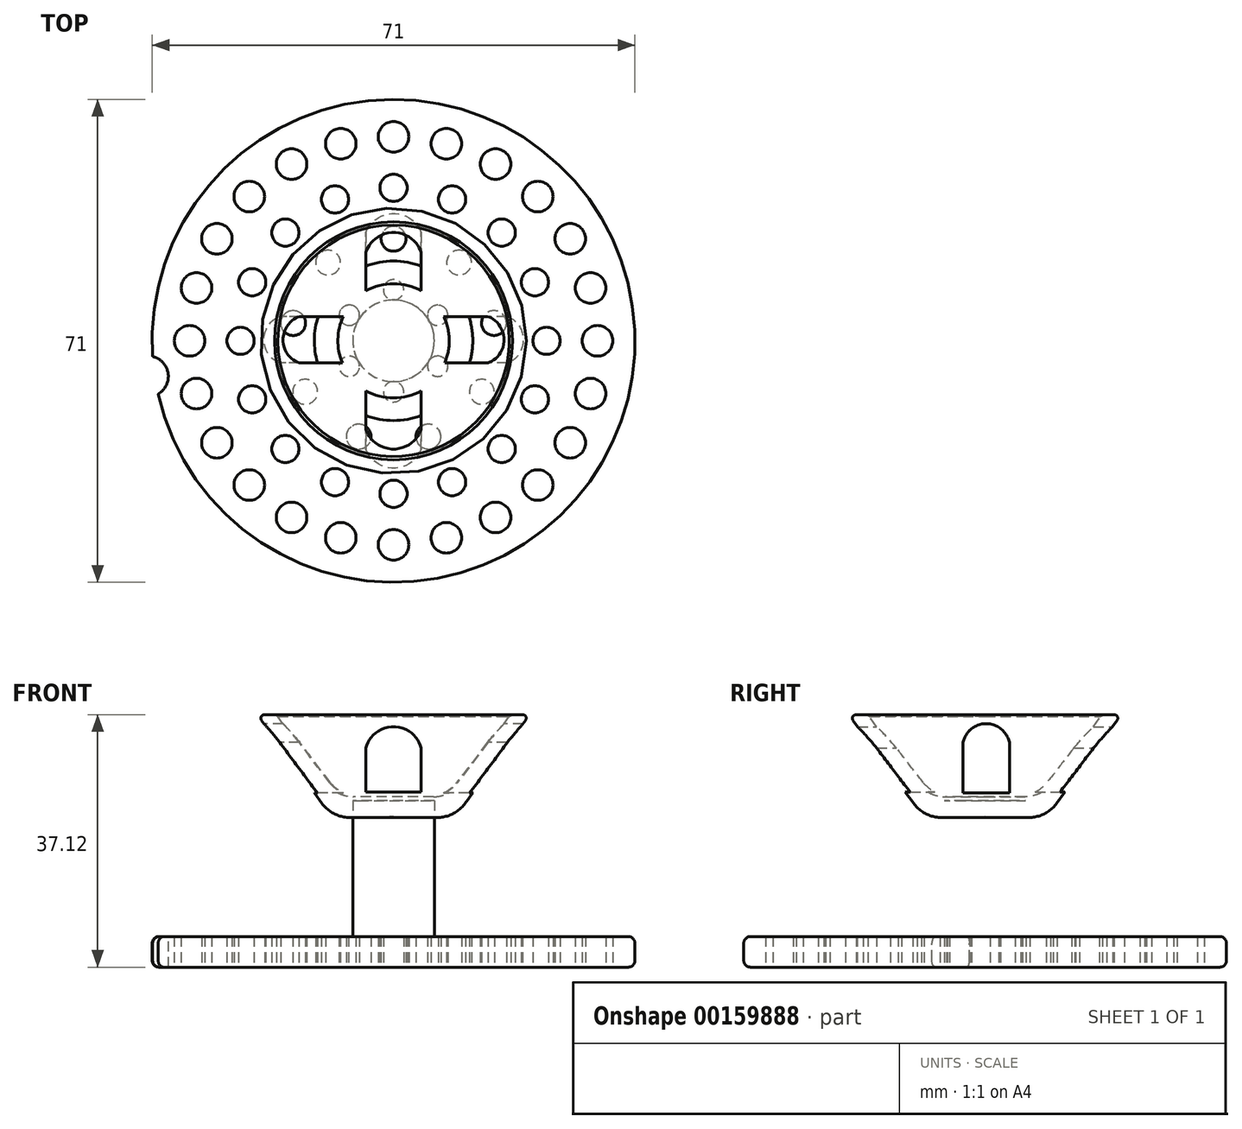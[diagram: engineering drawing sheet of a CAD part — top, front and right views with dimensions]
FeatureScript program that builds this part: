
annotation { "Feature Type Name" : "Feature", "Feature Type Description" : "" }
export const myFeature = defineFeature(function(context is Context, id is Id, definition is map)
    precondition{}
    {
        {
            var Q0;
            Q0=qCreatedBy(makeId("Top.planeOp"),FACE);
            var sketch = newSketch(context, id + "F0", { "sketchPlane" : qUnion([Q0])});
            skCircle(sketch, "E0", {"center": v(0, 0) * mm, "radius": 35.5 * mm});
            skSolve(sketch);
        }
        {
            var Q0;
            Q0=makeQuery(id+"F0.imprint","IMPRINT",FACE,{"disambiguationData":[TD([[makeQuery(id+"F0.imprint","IMPRINT",EDGE,{"derivedFrom":sQuery(id+"F0.wireOp",EDGE,"E0")}),1.0]])]});
            var sketch = newSketch(context, id + "F1", { "sketchPlane" : qUnion([Q0])});
            skCircle(sketch, "E1", {"center": v(0, 0) * mm, "radius": 7.5 * mm, "construction": true});
            skCircle(sketch, "E2", {"center": v(0, 7.5) * mm, "radius": 1.5 * mm});
            skCircle(sketch, "E3.1.1", {"center": v(-6.5, 3.75) * mm, "radius": 1.5 * mm});
            skCircle(sketch, "E3.2.1", {"center": v(-6.5, -3.75) * mm, "radius": 1.5 * mm});
            skCircle(sketch, "E3.3.1", {"center": v(0, -7.5) * mm, "radius": 1.5 * mm});
            skCircle(sketch, "E3.4.1", {"center": v(6.5, -3.75) * mm, "radius": 1.5 * mm});
            skCircle(sketch, "E3.5.1", {"center": v(6.5, 3.75) * mm, "radius": 1.5 * mm});
            skSolve(sketch);
        }
        {
            var Q0;
            Q0=makeQuery(id+"F0.imprint","IMPRINT",FACE,{"disambiguationData":[TD([[makeQuery(id+"F0.imprint","IMPRINT",EDGE,{"derivedFrom":sQuery(id+"F0.wireOp",EDGE,"E0")}),1.0]])]});
            var sketch = newSketch(context, id + "F2", { "sketchPlane" : qUnion([Q0])});
            skCircle(sketch, "E4", {"center": v(0, 0) * mm, "radius": 15 * mm, "construction": true});
            skCircle(sketch, "E5", {"center": v(0, 15) * mm, "radius": 1.83 * mm});
            skCircle(sketch, "E6.1.0", {"center": v(-9.64, 11.5) * mm, "radius": 1.83 * mm});
            skCircle(sketch, "E6.2.0", {"center": v(-14.77, 2.6) * mm, "radius": 1.83 * mm});
            skCircle(sketch, "E6.3.0", {"center": v(-13, -7.5) * mm, "radius": 1.83 * mm});
            skCircle(sketch, "E6.4.0", {"center": v(-5.13, -14.1) * mm, "radius": 1.83 * mm});
            skCircle(sketch, "E6.5.0", {"center": v(5.13, -14.1) * mm, "radius": 1.83 * mm});
            skCircle(sketch, "E6.6.0", {"center": v(13, -7.5) * mm, "radius": 1.83 * mm});
            skCircle(sketch, "E6.7.0", {"center": v(14.77, 2.6) * mm, "radius": 1.83 * mm});
            skCircle(sketch, "E6.8.0", {"center": v(9.64, 11.5) * mm, "radius": 1.83 * mm});
            skSolve(sketch);
        }
        {
            var Q0;
            Q0=makeQuery(id+"F0.imprint","IMPRINT",FACE,{"disambiguationData":[TD([[makeQuery(id+"F0.imprint","IMPRINT",EDGE,{"derivedFrom":sQuery(id+"F0.wireOp",EDGE,"E0")}),1.0]])]});
            var sketch = newSketch(context, id + "F3", { "sketchPlane" : qUnion([Q0])});
            skCircle(sketch, "E7", {"center": v(0, 0) * mm, "radius": 22.5 * mm, "construction": true});
            skCircle(sketch, "E8", {"center": v(0, 22.5) * mm, "radius": 2 * mm});
            skCircle(sketch, "E9.1.0", {"center": v(-8.61, 20.79) * mm, "radius": 2 * mm});
            skCircle(sketch, "E9.2.0", {"center": v(-15.9, 15.9) * mm, "radius": 2 * mm});
            skCircle(sketch, "E9.3.0", {"center": v(-20.79, 8.61) * mm, "radius": 2 * mm});
            skCircle(sketch, "E9.4.0", {"center": v(-22.5, 0) * mm, "radius": 2 * mm});
            skCircle(sketch, "E9.5.0", {"center": v(-20.79, -8.61) * mm, "radius": 2 * mm});
            skCircle(sketch, "E9.6.0", {"center": v(-15.9, -15.9) * mm, "radius": 2 * mm});
            skCircle(sketch, "E9.7.0", {"center": v(-8.61, -20.79) * mm, "radius": 2 * mm});
            skCircle(sketch, "E9.8.0", {"center": v(0, -22.5) * mm, "radius": 2 * mm});
            skCircle(sketch, "E9.9.0", {"center": v(8.61, -20.79) * mm, "radius": 2 * mm});
            skCircle(sketch, "E9.10.0", {"center": v(15.9, -15.9) * mm, "radius": 2 * mm});
            skCircle(sketch, "E9.11.0", {"center": v(20.79, -8.61) * mm, "radius": 2 * mm});
            skCircle(sketch, "E9.12.0", {"center": v(22.5, 0) * mm, "radius": 2 * mm});
            skCircle(sketch, "E9.13.0", {"center": v(20.79, 8.61) * mm, "radius": 2 * mm});
            skCircle(sketch, "E9.14.0", {"center": v(15.9, 15.9) * mm, "radius": 2 * mm});
            skCircle(sketch, "E9.15.0", {"center": v(8.61, 20.79) * mm, "radius": 2 * mm});
            skSolve(sketch);
        }
        {
            var Q0;
            Q0=makeQuery(id+"F0.imprint","IMPRINT",FACE,{"disambiguationData":[TD([[makeQuery(id+"F0.imprint","IMPRINT",EDGE,{"derivedFrom":sQuery(id+"F0.wireOp",EDGE,"E0")}),1.0]])]});
            var sketch = newSketch(context, id + "F4", { "sketchPlane" : qUnion([Q0])});
            skCircle(sketch, "E10", {"center": v(0, 0) * mm, "radius": 30 * mm, "construction": true});
            skCircle(sketch, "E11", {"center": v(0, 30) * mm, "radius": 2.25 * mm});
            skCircle(sketch, "E12.1.0", {"center": v(-7.76, 28.98) * mm, "radius": 2.25 * mm});
            skCircle(sketch, "E12.2.0", {"center": v(-15, 25.98) * mm, "radius": 2.25 * mm});
            skCircle(sketch, "E13.1.3.0", {"center": v(-21.21, 21.21) * mm, "radius": 2.25 * mm});
            skCircle(sketch, "E13.1.4.0", {"center": v(-25.98, 15) * mm, "radius": 2.25 * mm});
            skCircle(sketch, "E13.1.5.0", {"center": v(-28.98, 7.76) * mm, "radius": 2.25 * mm});
            skCircle(sketch, "E13.1.6.0", {"center": v(-30, 0) * mm, "radius": 2.25 * mm});
            skCircle(sketch, "E13.1.7.0", {"center": v(-28.98, -7.76) * mm, "radius": 2.25 * mm});
            skCircle(sketch, "E13.1.8.0", {"center": v(-25.98, -15) * mm, "radius": 2.25 * mm});
            skCircle(sketch, "E13.1.9.0", {"center": v(-21.21, -21.21) * mm, "radius": 2.25 * mm});
            skCircle(sketch, "E13.1.10.0", {"center": v(-15, -25.98) * mm, "radius": 2.25 * mm});
            skCircle(sketch, "E13.1.11.0", {"center": v(-7.76, -28.98) * mm, "radius": 2.25 * mm});
            skCircle(sketch, "E13.1.12.0", {"center": v(0, -30) * mm, "radius": 2.25 * mm});
            skCircle(sketch, "E13.1.13.0", {"center": v(7.76, -28.98) * mm, "radius": 2.25 * mm});
            skCircle(sketch, "E13.1.14.0", {"center": v(15, -25.98) * mm, "radius": 2.25 * mm});
            skCircle(sketch, "E13.1.15.0", {"center": v(21.21, -21.21) * mm, "radius": 2.25 * mm});
            skCircle(sketch, "E13.1.16.0", {"center": v(25.98, -15) * mm, "radius": 2.25 * mm});
            skCircle(sketch, "E13.1.17.0", {"center": v(28.98, -7.76) * mm, "radius": 2.25 * mm});
            skCircle(sketch, "E13.1.18.0", {"center": v(30, 0) * mm, "radius": 2.25 * mm});
            skCircle(sketch, "E13.1.19.0", {"center": v(28.98, 7.76) * mm, "radius": 2.25 * mm});
            skCircle(sketch, "E13.1.20.0", {"center": v(25.98, 15) * mm, "radius": 2.25 * mm});
            skCircle(sketch, "E13.1.21.0", {"center": v(21.21, 21.21) * mm, "radius": 2.25 * mm});
            skCircle(sketch, "E13.1.22.0", {"center": v(15, 25.98) * mm, "radius": 2.25 * mm});
            skCircle(sketch, "E13.1.23.0", {"center": v(7.76, 28.98) * mm, "radius": 2.25 * mm});
            skSolve(sketch);
        }
        {
            var Q0;
            Q0=qSketchRegion(id+"F4",true);
            extrude(context, id + "F5", {"entities" : qUnion([Q0]), "depth" : 5 * mm});
        }
        {
            var Q0;
            Q0=qSketchRegion(id+"F3",true);
            extrude(context, id + "F6", {"entities" : qUnion([Q0]), "depth" : 5 * mm});
        }
        {
            var Q0;
            Q0=qSketchRegion(id+"F2",true);
            extrude(context, id + "F7", {"entities" : qUnion([Q0]), "depth" : 5 * mm});
        }
        {
            var Q0;
            Q0=qSketchRegion(id+"F1",true);
            extrude(context, id + "F8", {"entities" : qUnion([Q0]), "depth" : 5 * mm});
        }
        {
            var Q0;
            Q0=qSketchRegion(id+"F0",true);
            extrude(context, id + "F9", {"entities" : qUnion([Q0]), "depth" : 4.5 * mm});
        }
        {
            var Q0;
            Q0=makeQuery(id+"F5.opExtrude","SWEPT_BODY",BODY,{"disambiguationData":[OSD([sQuery(id+"F4.wireOp",EDGE,"E11")])]});
            var Q1;
            Q1=makeQuery(id+"F5.opExtrude","SWEPT_BODY",BODY,{"disambiguationData":[OSD([sQuery(id+"F4.wireOp",EDGE,"E13.1.3.0")])]});
            var Q2;
            Q2=makeQuery(id+"F5.opExtrude","SWEPT_BODY",BODY,{"disambiguationData":[OSD([sQuery(id+"F4.wireOp",EDGE,"E13.1.7.0")])]});
            var Q3;
            Q3=makeQuery(id+"F5.opExtrude","SWEPT_BODY",BODY,{"disambiguationData":[OSD([sQuery(id+"F4.wireOp",EDGE,"E12.1.0")])]});
            var Q4;
            Q4=makeQuery(id+"F5.opExtrude","SWEPT_BODY",BODY,{"disambiguationData":[OSD([sQuery(id+"F4.wireOp",EDGE,"E12.2.0")])]});
            var Q5;
            Q5=makeQuery(id+"F5.opExtrude","SWEPT_BODY",BODY,{"disambiguationData":[OSD([sQuery(id+"F4.wireOp",EDGE,"E13.1.4.0")])]});
            var Q6;
            Q6=makeQuery(id+"F5.opExtrude","SWEPT_BODY",BODY,{"disambiguationData":[OSD([sQuery(id+"F4.wireOp",EDGE,"E13.1.5.0")])]});
            var Q7;
            Q7=makeQuery(id+"F5.opExtrude","SWEPT_BODY",BODY,{"disambiguationData":[OSD([sQuery(id+"F4.wireOp",EDGE,"E13.1.6.0")])]});
            var Q8;
            Q8=makeQuery(id+"F5.opExtrude","SWEPT_BODY",BODY,{"disambiguationData":[OSD([sQuery(id+"F4.wireOp",EDGE,"E13.1.8.0")])]});
            var Q9;
            Q9=makeQuery(id+"F5.opExtrude","SWEPT_BODY",BODY,{"disambiguationData":[OSD([sQuery(id+"F4.wireOp",EDGE,"E13.1.9.0")])]});
            var Q10;
            Q10=makeQuery(id+"F5.opExtrude","SWEPT_BODY",BODY,{"disambiguationData":[OSD([sQuery(id+"F4.wireOp",EDGE,"E13.1.10.0")])]});
            var Q11;
            Q11=makeQuery(id+"F5.opExtrude","SWEPT_BODY",BODY,{"disambiguationData":[OSD([sQuery(id+"F4.wireOp",EDGE,"E13.1.11.0")])]});
            var Q12;
            Q12=makeQuery(id+"F5.opExtrude","SWEPT_BODY",BODY,{"disambiguationData":[OSD([sQuery(id+"F4.wireOp",EDGE,"E13.1.12.0")])]});
            var Q13;
            Q13=makeQuery(id+"F5.opExtrude","SWEPT_BODY",BODY,{"disambiguationData":[OSD([sQuery(id+"F4.wireOp",EDGE,"E13.1.13.0")])]});
            var Q14;
            Q14=makeQuery(id+"F5.opExtrude","SWEPT_BODY",BODY,{"disambiguationData":[OSD([sQuery(id+"F4.wireOp",EDGE,"E13.1.14.0")])]});
            var Q15;
            Q15=makeQuery(id+"F5.opExtrude","SWEPT_BODY",BODY,{"disambiguationData":[OSD([sQuery(id+"F4.wireOp",EDGE,"E13.1.15.0")])]});
            var Q16;
            Q16=makeQuery(id+"F5.opExtrude","SWEPT_BODY",BODY,{"disambiguationData":[OSD([sQuery(id+"F4.wireOp",EDGE,"E13.1.16.0")])]});
            var Q17;
            Q17=makeQuery(id+"F5.opExtrude","SWEPT_BODY",BODY,{"disambiguationData":[OSD([sQuery(id+"F4.wireOp",EDGE,"E13.1.17.0")])]});
            var Q18;
            Q18=makeQuery(id+"F5.opExtrude","SWEPT_BODY",BODY,{"disambiguationData":[OSD([sQuery(id+"F4.wireOp",EDGE,"E13.1.18.0")])]});
            var Q19;
            Q19=makeQuery(id+"F5.opExtrude","SWEPT_BODY",BODY,{"disambiguationData":[OSD([sQuery(id+"F4.wireOp",EDGE,"E13.1.19.0")])]});
            var Q20;
            Q20=makeQuery(id+"F5.opExtrude","SWEPT_BODY",BODY,{"disambiguationData":[OSD([sQuery(id+"F4.wireOp",EDGE,"E13.1.20.0")])]});
            var Q21;
            Q21=makeQuery(id+"F5.opExtrude","SWEPT_BODY",BODY,{"disambiguationData":[OSD([sQuery(id+"F4.wireOp",EDGE,"E13.1.21.0")])]});
            var Q22;
            Q22=makeQuery(id+"F5.opExtrude","SWEPT_BODY",BODY,{"disambiguationData":[OSD([sQuery(id+"F4.wireOp",EDGE,"E13.1.22.0")])]});
            var Q23;
            Q23=makeQuery(id+"F5.opExtrude","SWEPT_BODY",BODY,{"disambiguationData":[OSD([sQuery(id+"F4.wireOp",EDGE,"E13.1.23.0")])]});
            var Q24;
            Q24=makeQuery(id+"F6.opExtrude","SWEPT_BODY",BODY,{"disambiguationData":[OSD([sQuery(id+"F3.wireOp",EDGE,"E9.15.0")])]});
            var Q25;
            Q25=makeQuery(id+"F6.opExtrude","SWEPT_BODY",BODY,{"disambiguationData":[OSD([sQuery(id+"F3.wireOp",EDGE,"E8")])]});
            var Q26;
            Q26=makeQuery(id+"F6.opExtrude","SWEPT_BODY",BODY,{"disambiguationData":[OSD([sQuery(id+"F3.wireOp",EDGE,"E9.1.0")])]});
            var Q27;
            Q27=makeQuery(id+"F6.opExtrude","SWEPT_BODY",BODY,{"disambiguationData":[OSD([sQuery(id+"F3.wireOp",EDGE,"E9.2.0")])]});
            var Q28;
            Q28=makeQuery(id+"F6.opExtrude","SWEPT_BODY",BODY,{"disambiguationData":[OSD([sQuery(id+"F3.wireOp",EDGE,"E9.3.0")])]});
            var Q29;
            Q29=makeQuery(id+"F6.opExtrude","SWEPT_BODY",BODY,{"disambiguationData":[OSD([sQuery(id+"F3.wireOp",EDGE,"E9.4.0")])]});
            var Q30;
            Q30=makeQuery(id+"F6.opExtrude","SWEPT_BODY",BODY,{"disambiguationData":[OSD([sQuery(id+"F3.wireOp",EDGE,"E9.5.0")])]});
            var Q31;
            Q31=makeQuery(id+"F6.opExtrude","SWEPT_BODY",BODY,{"disambiguationData":[OSD([sQuery(id+"F3.wireOp",EDGE,"E9.6.0")])]});
            var Q32;
            Q32=makeQuery(id+"F6.opExtrude","SWEPT_BODY",BODY,{"disambiguationData":[OSD([sQuery(id+"F3.wireOp",EDGE,"E9.7.0")])]});
            var Q33;
            Q33=makeQuery(id+"F6.opExtrude","SWEPT_BODY",BODY,{"disambiguationData":[OSD([sQuery(id+"F3.wireOp",EDGE,"E9.8.0")])]});
            var Q34;
            Q34=makeQuery(id+"F6.opExtrude","SWEPT_BODY",BODY,{"disambiguationData":[OSD([sQuery(id+"F3.wireOp",EDGE,"E9.9.0")])]});
            var Q35;
            Q35=makeQuery(id+"F6.opExtrude","SWEPT_BODY",BODY,{"disambiguationData":[OSD([sQuery(id+"F3.wireOp",EDGE,"E9.10.0")])]});
            var Q36;
            Q36=makeQuery(id+"F6.opExtrude","SWEPT_BODY",BODY,{"disambiguationData":[OSD([sQuery(id+"F3.wireOp",EDGE,"E9.11.0")])]});
            var Q37;
            Q37=makeQuery(id+"F6.opExtrude","SWEPT_BODY",BODY,{"disambiguationData":[OSD([sQuery(id+"F3.wireOp",EDGE,"E9.12.0")])]});
            var Q38;
            Q38=makeQuery(id+"F6.opExtrude","SWEPT_BODY",BODY,{"disambiguationData":[OSD([sQuery(id+"F3.wireOp",EDGE,"E9.13.0")])]});
            var Q39;
            Q39=makeQuery(id+"F6.opExtrude","SWEPT_BODY",BODY,{"disambiguationData":[OSD([sQuery(id+"F3.wireOp",EDGE,"E9.14.0")])]});
            var Q40;
            Q40=makeQuery(id+"F7.opExtrude","SWEPT_BODY",BODY,{"disambiguationData":[OSD([sQuery(id+"F2.wireOp",EDGE,"E6.8.0")])]});
            var Q41;
            Q41=makeQuery(id+"F7.opExtrude","SWEPT_BODY",BODY,{"disambiguationData":[OSD([sQuery(id+"F2.wireOp",EDGE,"E6.7.0")])]});
            var Q42;
            Q42=makeQuery(id+"F7.opExtrude","SWEPT_BODY",BODY,{"disambiguationData":[OSD([sQuery(id+"F2.wireOp",EDGE,"E6.6.0")])]});
            var Q43;
            Q43=makeQuery(id+"F7.opExtrude","SWEPT_BODY",BODY,{"disambiguationData":[OSD([sQuery(id+"F2.wireOp",EDGE,"E6.5.0")])]});
            var Q44;
            Q44=makeQuery(id+"F7.opExtrude","SWEPT_BODY",BODY,{"disambiguationData":[OSD([sQuery(id+"F2.wireOp",EDGE,"E6.4.0")])]});
            var Q45;
            Q45=makeQuery(id+"F7.opExtrude","SWEPT_BODY",BODY,{"disambiguationData":[OSD([sQuery(id+"F2.wireOp",EDGE,"E6.3.0")])]});
            var Q46;
            Q46=makeQuery(id+"F7.opExtrude","SWEPT_BODY",BODY,{"disambiguationData":[OSD([sQuery(id+"F2.wireOp",EDGE,"E6.2.0")])]});
            var Q47;
            Q47=makeQuery(id+"F7.opExtrude","SWEPT_BODY",BODY,{"disambiguationData":[OSD([sQuery(id+"F2.wireOp",EDGE,"E6.1.0")])]});
            var Q48;
            Q48=makeQuery(id+"F7.opExtrude","SWEPT_BODY",BODY,{"disambiguationData":[OSD([sQuery(id+"F2.wireOp",EDGE,"E5")])]});
            var Q49;
            Q49=makeQuery(id+"F8.opExtrude","SWEPT_BODY",BODY,{"disambiguationData":[OSD([sQuery(id+"F1.wireOp",EDGE,"E2")])]});
            var Q50;
            Q50=makeQuery(id+"F8.opExtrude","SWEPT_BODY",BODY,{"disambiguationData":[OSD([sQuery(id+"F1.wireOp",EDGE,"E3.5.1")])]});
            var Q51;
            Q51=makeQuery(id+"F8.opExtrude","SWEPT_BODY",BODY,{"disambiguationData":[OSD([sQuery(id+"F1.wireOp",EDGE,"E3.4.1")])]});
            var Q52;
            Q52=makeQuery(id+"F8.opExtrude","SWEPT_BODY",BODY,{"disambiguationData":[OSD([sQuery(id+"F1.wireOp",EDGE,"E3.3.1")])]});
            var Q53;
            Q53=makeQuery(id+"F8.opExtrude","SWEPT_BODY",BODY,{"disambiguationData":[OSD([sQuery(id+"F1.wireOp",EDGE,"E3.2.1")])]});
            var Q54;
            Q54=makeQuery(id+"F8.opExtrude","SWEPT_BODY",BODY,{"disambiguationData":[OSD([sQuery(id+"F1.wireOp",EDGE,"E3.1.1")])]});
            var Q55;
            Q55=makeQuery(id+"F9.opExtrude","SWEPT_BODY",BODY,{"disambiguationData":[OSD([sQuery(id+"F0.wireOp",EDGE,"E0")])]});
            booleanBodies(context, id + "F10", {"operationType" : BooleanOperationType.SUBTRACTION, "tools" : qUnion([Q0, Q1, Q2, Q3, Q4, Q5, Q6, Q7, Q8, Q9, Q10, Q11, Q12, Q13, Q14, Q15, Q16, Q17, Q18, Q19, Q20, Q21, Q22, Q23, Q24, Q25, Q26, Q27, Q28, Q29, Q30, Q31, Q32, Q33, Q34, Q35, Q36, Q37, Q38, Q39, Q40, Q41, Q42, Q43, Q44, Q45, Q46, Q47, Q48, Q49, Q50, Q51, Q52, Q53, Q54]), "targets" : qUnion([Q55])});
        }
        {
            var Q0;
            Q0=makeQuery(id+"F9.opExtrude","CAP_EDGE",EDGE,{"disambiguationData":[OSD([sQuery(id+"F0.wireOp",EDGE,"E0")])],"isStart":true});
            var Q1;
            Q1=makeQuery(id+"F9.opExtrude","CAP_EDGE",EDGE,{"disambiguationData":[OSD([sQuery(id+"F0.wireOp",EDGE,"E0")])],"isStart":false});
            fillet(context, id + "F11", {"entities" : qUnion([Q0, Q1]), "radius" : 1 * mm, "tangentPropagation" : true, "allowEdgeOverflow" : false});
        }
        {
            var Q0;
            Q0=makeQuery(id+"F9.opExtrude","CAP_FACE",FACE,{"disambiguationData":[OSD([sQuery(id+"F0.wireOp",EDGE,"E0")])],"isStart":false});
            var sketch = newSketch(context, id + "F12", { "sketchPlane" : qUnion([Q0])});
            skCircle(sketch, "E14", {"center": v(0, 0) * mm, "radius": 6 * mm});
            skSolve(sketch);
        }
        {
            var Q0;
            Q0=makeQuery(id+"F12.imprint","IMPRINT",FACE,{"disambiguationData":[TD([[makeQuery(id+"F12.imprint","IMPRINT",EDGE,{"derivedFrom":sQuery(id+"F12.wireOp",EDGE,"E14")}),1.0]])]});
            extrude(context, id + "F13", {"entities" : qUnion([Q0]), "operationType" : NewBodyOperationType.ADD, "depth" : 20 * mm, "offsetDistance" : 25 * mm});
        }
        {
            var Q0;
            Q0=makeQuery(id+"F9.opExtrude","CAP_FACE",FACE,{"disambiguationData":[OSD([sQuery(id+"F0.wireOp",EDGE,"E0")])],"isStart":false});
            var sketch = newSketch(context, id + "F14", { "sketchPlane" : qUnion([Q0])});
            skCircle(sketch, "E15", {"center": v(0, 0) * mm, "radius": 36.5 * mm, "construction": true});
            skCircle(sketch, "E16", {"center": v(-36.12, -5.23) * mm, "radius": 3 * mm});
            skSolve(sketch);
        }
        {
            var Q0;
            Q0=makeQuery(id+"F14.imprint","IMPRINT",FACE,{"disambiguationData":[TD([[makeQuery(id+"F14.imprint","IMPRINT",EDGE,{"derivedFrom":sQuery(id+"F14.wireOp",EDGE,"E16")}),1.0]])]});
            extrude(context, id + "F15", {"entities" : qUnion([Q0]), "operationType" : NewBodyOperationType.REMOVE, "oppositeDirection" : true, "depth" : 25 * mm});
        }
        {
            var Q0;
            Q0=qCreatedBy(makeId("Front.planeOp"),FACE);
            var sketch = newSketch(context, id + "F16", { "sketchPlane" : qUnion([Q0])});
            skLineSegment(sketch, "E17", {"start": v(0, 64.6) * mm, "end": v(0, 86.12) * mm, "construction": true});
            skLineSegment(sketch, "E18", {"start": v(-20, 85.12) * mm, "end": v(-9, 69.99) * mm});
            skLineSegment(sketch, "E19", {"start": v(0, 70.12) * mm, "end": v(0, 86.12) * mm});
            skLineSegment(sketch, "E20", {"start": v(-20, 85.12) * mm, "end": v(-17.2, 85.12) * mm});
            skLineSegment(sketch, "E21", {"start": v(-17.2, 85.12) * mm, "end": v(-8.44, 73.07) * mm});
            skLineSegment(sketch, "E22", {"start": v(-8.44, 73.07) * mm, "end": v(0, 73.07) * mm});
            skLineSegment(sketch, "E23", {"start": v(-9, 69.99) * mm, "end": v(0, 70.12) * mm});
            skSolve(sketch);
        }
        {
            var Q0;
            Q0=makeQuery(id+"F16.imprint","IMPRINT",FACE,{"disambiguationData":[TD([[makeQuery(id+"F16.imprint","IMPRINT",EDGE,{"derivedFrom":sQuery(id+"F16.wireOp",EDGE,"E18")}),1.0]])]});
            var Q1;
            Q1=sQuery(id+"F16.wireOp",EDGE,"E19");
            revolve(context, id + "F17", {"operationType" : NewBodyOperationType.ADD, "surfaceOperationType" : NewSurfaceOperationType.NEW, "entities" : qUnion([Q0]), "axis" : qUnion([Q1]), "revolveType" : RevolveType.FULL});
        }
        {
            var Q0;
            Q0=makeQuery(id+"F17.opRevolve","SWEPT_BODY",BODY,{"disambiguationData":[OSD([sQuery(id+"F16.wireOp",EDGE,"E18"),sQuery(id+"F16.wireOp",EDGE,"ekqP7qBP-ulQC-kSXt-n5Og-ePe3p9eNB1yX"),sQuery(id+"F16.wireOp",EDGE,"E19"),sQuery(id+"F16.wireOp",EDGE,"E20"),sQuery(id+"F16.wireOp",EDGE,"E21"),sQuery(id+"F16.wireOp",EDGE,"E22")])]});
            transform(context, id + "F18", {"entities" : qUnion([Q0]), "transformType" : TransformType.TRANSLATION_3D, "dx" : 0 * mm, "dy" : 0 * mm, "dz" : -48 * mm, "makeCopy" : false});
        }
        {
            var Q0;
            Q0=qCreatedBy(makeId("Front.planeOp"),FACE);
            var sketch = newSketch(context, id + "F19", { "sketchPlane" : qUnion([Q0])});
            skLineSegment(sketch, "E24.bottom", {"start": v(4.06, 25.75) * mm, "end": v(-4.06, 25.75) * mm});
            skLineSegment(sketch, "E24.top", {"start": v(4.06, 32.22) * mm, "end": v(-4.06, 32.22) * mm});
            skLineSegment(sketch, "E24.left", {"start": v(4.06, 25.75) * mm, "end": v(4.06, 32.22) * mm});
            skLineSegment(sketch, "E24.right", {"start": v(-4.06, 25.75) * mm, "end": v(-4.06, 32.22) * mm});
            skPoint(sketch, "E24.middle", {"position": v(0, 28.98) * mm});
            skLineSegment(sketch, "E25", {"start": v(0, 59.77) * mm, "end": v(0, 0) * mm, "construction": true});
            skArc(sketch, "E26", {"start": v(4.06, 32.22) * mm, "mid": v(0, 35.37) * mm, "end": v(-4.06, 32.22) * mm});
            skSolve(sketch);
        }
        {
            var Q0;
            Q0=qSketchRegion(id+"F19",true);
            extrude(context, id + "F20", {"entities" : qUnion([Q0]), "endBound" : BoundingType.SYMMETRIC, "depth" : 45 * mm, "offsetDistance" : 25 * mm});
        }
        {
            var Q0;
            {var subQ0=sQuery(id+"F16.wireOp",EDGE,"E20");var subQ1=sQuery(id+"F16.wireOp",EDGE,"E21");Q0=makeQuery(id+"F24O2oq0PfPqQpG_3.opBoolean","SPLIT",EDGE,{"disambiguationData":[TD([makeQuery(id+"FJ4bphDz8gUAr4i_3.opPattern","COPY",FACE,{"derivedFrom":makeQuery(id+"F20.opExtrude","SWEPT_FACE",FACE,{"disambiguationData":[OSD([sQuery(id+"F19.wireOp",EDGE,"E24.left")])]}),"instanceName":"2"})])],"derivedFrom":makeQuery(id+"F17.opRevolve","SWEPT_EDGE",EDGE,{"disambiguationData":[OSD([subQ0,subQ1])]})});}
            var Q1;
            {var subQ0=sQuery(id+"F16.wireOp",EDGE,"E20");var subQ1=sQuery(id+"F16.wireOp",EDGE,"E21");Q1=makeQuery(id+"F24O2oq0PfPqQpG_3.opBoolean","SPLIT",EDGE,{"disambiguationData":[TD([makeQuery(id+"FJ4bphDz8gUAr4i_3.opPattern","COPY",FACE,{"derivedFrom":makeQuery(id+"F20.opExtrude","SWEPT_FACE",FACE,{"disambiguationData":[OSD([sQuery(id+"F19.wireOp",EDGE,"E24.left")])]}),"instanceName":"1"})])],"derivedFrom":makeQuery(id+"F17.opRevolve","SWEPT_EDGE",EDGE,{"disambiguationData":[OSD([subQ0,subQ1])]})});}
            var Q2;
            {var subQ0=sQuery(id+"F16.wireOp",EDGE,"E20");var subQ1=sQuery(id+"F16.wireOp",EDGE,"E21");Q2=makeQuery(id+"F24O2oq0PfPqQpG_3.opBoolean","SPLIT",EDGE,{"disambiguationData":[TD([makeQuery(id+"F20.opExtrude","SWEPT_FACE",FACE,{"disambiguationData":[OSD([sQuery(id+"F19.wireOp",EDGE,"E24.left")])]})])],"derivedFrom":makeQuery(id+"F17.opRevolve","SWEPT_EDGE",EDGE,{"disambiguationData":[OSD([subQ0,subQ1])]})});}
            var Q3;
            {var subQ0=sQuery(id+"F16.wireOp",EDGE,"E20");var subQ1=sQuery(id+"F16.wireOp",EDGE,"E21");Q3=makeQuery(id+"F24O2oq0PfPqQpG_3.opBoolean","SPLIT",EDGE,{"disambiguationData":[TD([makeQuery(id+"F20.opExtrude","SWEPT_FACE",FACE,{"disambiguationData":[OSD([sQuery(id+"F19.wireOp",EDGE,"E24.right")])]})])],"derivedFrom":makeQuery(id+"F17.opRevolve","SWEPT_EDGE",EDGE,{"disambiguationData":[OSD([subQ0,subQ1])]})});}
            var Q4;
            {var subQ0=sQuery(id+"F16.wireOp",EDGE,"E20");var subQ1=sQuery(id+"F16.wireOp",EDGE,"E21");Q4=makeQuery(id+"F24O2oq0PfPqQpG_3.opBoolean","SPLIT",EDGE,{"disambiguationData":[TD([makeQuery(id+"FJ4bphDz8gUAr4i_3.opPattern","COPY",FACE,{"derivedFrom":makeQuery(id+"F20.opExtrude","SWEPT_FACE",FACE,{"disambiguationData":[OSD([sQuery(id+"F19.wireOp",EDGE,"E24.left")])]}),"instanceName":"4"})])],"derivedFrom":makeQuery(id+"F17.opRevolve","SWEPT_EDGE",EDGE,{"disambiguationData":[OSD([subQ0,subQ1])]})});}
            var Q5;
            {var subQ0=sQuery(id+"F16.wireOp",EDGE,"E20");var subQ1=sQuery(id+"F16.wireOp",EDGE,"E21");Q5=makeQuery(id+"F24O2oq0PfPqQpG_3.opBoolean","SPLIT",EDGE,{"disambiguationData":[TD([makeQuery(id+"FJ4bphDz8gUAr4i_3.opPattern","COPY",FACE,{"derivedFrom":makeQuery(id+"F20.opExtrude","SWEPT_FACE",FACE,{"disambiguationData":[OSD([sQuery(id+"F19.wireOp",EDGE,"E24.left")])]}),"instanceName":"3"})])],"derivedFrom":makeQuery(id+"F17.opRevolve","SWEPT_EDGE",EDGE,{"disambiguationData":[OSD([subQ0,subQ1])]})});}
            chamfer(context, id + "F21", {"entities" : qUnion([Q0, Q1, Q2, Q3, Q4, Q5]), "width" : 0.6 * mm, "tangentPropagation" : true});
        }
        {
            var Q0;
            {var subQ0=sQuery(id+"F16.wireOp",EDGE,"E18");var subQ1=sQuery(id+"F16.wireOp",EDGE,"E20");Q0=makeQuery(id+"F24O2oq0PfPqQpG_3.opBoolean","SPLIT",EDGE,{"disambiguationData":[TD([makeQuery(id+"FJ4bphDz8gUAr4i_3.opPattern","COPY",FACE,{"derivedFrom":makeQuery(id+"F20.opExtrude","SWEPT_FACE",FACE,{"disambiguationData":[OSD([sQuery(id+"F19.wireOp",EDGE,"E24.left")])]}),"instanceName":"2"})])],"derivedFrom":makeQuery(id+"F17.opRevolve","SWEPT_EDGE",EDGE,{"disambiguationData":[OSD([subQ0,subQ1])]})});}
            var Q1;
            {var subQ0=sQuery(id+"F16.wireOp",EDGE,"E18");var subQ1=sQuery(id+"F16.wireOp",EDGE,"E20");Q1=makeQuery(id+"F24O2oq0PfPqQpG_3.opBoolean","SPLIT",EDGE,{"disambiguationData":[TD([makeQuery(id+"FJ4bphDz8gUAr4i_3.opPattern","COPY",FACE,{"derivedFrom":makeQuery(id+"F20.opExtrude","SWEPT_FACE",FACE,{"disambiguationData":[OSD([sQuery(id+"F19.wireOp",EDGE,"E24.left")])]}),"instanceName":"1"})])],"derivedFrom":makeQuery(id+"F17.opRevolve","SWEPT_EDGE",EDGE,{"disambiguationData":[OSD([subQ0,subQ1])]})});}
            var Q2;
            {var subQ0=sQuery(id+"F16.wireOp",EDGE,"E18");var subQ1=sQuery(id+"F16.wireOp",EDGE,"E20");Q2=makeQuery(id+"F24O2oq0PfPqQpG_3.opBoolean","SPLIT",EDGE,{"disambiguationData":[TD([makeQuery(id+"F20.opExtrude","SWEPT_FACE",FACE,{"disambiguationData":[OSD([sQuery(id+"F19.wireOp",EDGE,"E24.left")])]})])],"derivedFrom":makeQuery(id+"F17.opRevolve","SWEPT_EDGE",EDGE,{"disambiguationData":[OSD([subQ0,subQ1])]})});}
            var Q3;
            {var subQ0=sQuery(id+"F16.wireOp",EDGE,"E18");var subQ1=sQuery(id+"F16.wireOp",EDGE,"E20");Q3=makeQuery(id+"F24O2oq0PfPqQpG_3.opBoolean","SPLIT",EDGE,{"disambiguationData":[TD([makeQuery(id+"F20.opExtrude","SWEPT_FACE",FACE,{"disambiguationData":[OSD([sQuery(id+"F19.wireOp",EDGE,"E24.right")])]})])],"derivedFrom":makeQuery(id+"F17.opRevolve","SWEPT_EDGE",EDGE,{"disambiguationData":[OSD([subQ0,subQ1])]})});}
            var Q4;
            {var subQ0=sQuery(id+"F16.wireOp",EDGE,"E18");var subQ1=sQuery(id+"F16.wireOp",EDGE,"E20");Q4=makeQuery(id+"F24O2oq0PfPqQpG_3.opBoolean","SPLIT",EDGE,{"disambiguationData":[TD([makeQuery(id+"FJ4bphDz8gUAr4i_3.opPattern","COPY",FACE,{"derivedFrom":makeQuery(id+"F20.opExtrude","SWEPT_FACE",FACE,{"disambiguationData":[OSD([sQuery(id+"F19.wireOp",EDGE,"E24.left")])]}),"instanceName":"4"})])],"derivedFrom":makeQuery(id+"F17.opRevolve","SWEPT_EDGE",EDGE,{"disambiguationData":[OSD([subQ0,subQ1])]})});}
            var Q5;
            {var subQ0=sQuery(id+"F16.wireOp",EDGE,"E18");var subQ1=sQuery(id+"F16.wireOp",EDGE,"E20");Q5=makeQuery(id+"F24O2oq0PfPqQpG_3.opBoolean","SPLIT",EDGE,{"disambiguationData":[TD([makeQuery(id+"FJ4bphDz8gUAr4i_3.opPattern","COPY",FACE,{"derivedFrom":makeQuery(id+"F20.opExtrude","SWEPT_FACE",FACE,{"disambiguationData":[OSD([sQuery(id+"F19.wireOp",EDGE,"E24.left")])]}),"instanceName":"3"})])],"derivedFrom":makeQuery(id+"F17.opRevolve","SWEPT_EDGE",EDGE,{"disambiguationData":[OSD([subQ0,subQ1])]})});}
            fillet(context, id + "F22", {"entities" : qUnion([Q0, Q1, Q2, Q3, Q4, Q5]), "tangentPropagation" : true, "radius" : .5 * mm, "defaultsChanged" : false, "vertexSettings" : [], "allowEdgeOverflow" : false});
        }
        {
            var Q0;
            Q0=makeQuery(id+"F17.opRevolve","SWEPT_EDGE",EDGE,{"disambiguationData":[OSD([sQuery(id+"F16.wireOp",EDGE,"E18"),sQuery(id+"F16.wireOp",EDGE,"E23")])]});
            fillet(context, id + "F23", {"entities" : qUnion([Q0]), "tangentPropagation" : true, "radius" : 5 * mm, "defaultsChanged" : false, "vertexSettings" : [], "allowEdgeOverflow" : false});
        }
        {
            var Q0;
            Q0=makeQuery(id+"F17.opRevolve","SWEPT_EDGE",EDGE,{"disambiguationData":[OSD([sQuery(id+"F16.wireOp",EDGE,"E21"),sQuery(id+"F16.wireOp",EDGE,"E22")])]});
            fillet(context, id + "F24", {"entities" : qUnion([Q0]), "tangentPropagation" : true, "radius" : 5 * mm, "defaultsChanged" : false, "vertexSettings" : [], "allowEdgeOverflow" : false});
        }
        {
            var Q0;
            Q0=qCreatedBy(makeId("Right.planeOp"),FACE);
            var sketch = newSketch(context, id + "F25", { "sketchPlane" : qUnion([Q0])});
            skLineSegment(sketch, "E27.bottom", {"start": v(3.57, 32.66) * mm, "end": v(-3.23, 32.66) * mm});
            skLineSegment(sketch, "E27.top", {"start": v(3.57, 25.23) * mm, "end": v(-3.23, 25.23) * mm});
            skLineSegment(sketch, "E27.left", {"start": v(3.57, 32.66) * mm, "end": v(3.57, 25.23) * mm});
            skLineSegment(sketch, "E27.right", {"start": v(-3.23, 32.66) * mm, "end": v(-3.23, 25.23) * mm});
            skArc(sketch, "E28", {"start": v(3.57, 32.66) * mm, "mid": v(0.17, 35.41) * mm, "end": v(-3.23, 32.66) * mm});
            skSolve(sketch);
        }
        {
            var Q0;
            Q0=qSketchRegion(id+"F25",true);
            extrude(context, id + "F26", {"entities" : qUnion([Q0]), "endBound" : BoundingType.SYMMETRIC, "depth" : 45 * mm, "offsetDistance" : 25 * mm});
        }
        {
            var Q0;
            Q0=makeQuery(id+"F26.opExtrude","SWEPT_BODY",BODY,{"disambiguationData":[OSD([sQuery(id+"F25.wireOp",EDGE,"E27.bottom"),sQuery(id+"F25.wireOp",EDGE,"E27.top"),sQuery(id+"F25.wireOp",EDGE,"E27.left"),sQuery(id+"F25.wireOp",EDGE,"E27.right")])]});
            transform(context, id + "F27", {"entities" : qUnion([Q0]), "transformType" : TransformType.TRANSLATION_3D, "dx" : 0 * mm, "dy" : 0 * mm, "dz" : 0.4 * mm, "makeCopy" : false});
        }
        {
            var Q0;
            Q0=makeQuery(id+"F20.opExtrude","SWEPT_BODY",BODY,{"disambiguationData":[OSD([sQuery(id+"F19.wireOp",EDGE,"E24.bottom"),sQuery(id+"F19.wireOp",EDGE,"E24.top"),sQuery(id+"F19.wireOp",EDGE,"E24.left"),sQuery(id+"F19.wireOp",EDGE,"E24.right")])]});
            var Q1;
            Q1=makeQuery(id+"F26.opExtrude","SWEPT_BODY",BODY,{"disambiguationData":[OSD([sQuery(id+"F25.wireOp",EDGE,"E27.bottom"),sQuery(id+"F25.wireOp",EDGE,"E27.top"),sQuery(id+"F25.wireOp",EDGE,"E27.left"),sQuery(id+"F25.wireOp",EDGE,"E27.right")])]});
            var Q2;
            Q2=makeQuery(id+"F17.opRevolve","SWEPT_BODY",BODY,{"disambiguationData":[OSD([sQuery(id+"F16.wireOp",EDGE,"E18"),sQuery(id+"F16.wireOp",EDGE,"E19"),sQuery(id+"F16.wireOp",EDGE,"E20"),sQuery(id+"F16.wireOp",EDGE,"E21"),sQuery(id+"F16.wireOp",EDGE,"E22"),sQuery(id+"F16.wireOp",EDGE,"E23")])]});
            booleanBodies(context, id + "F28", {"operationType" : BooleanOperationType.SUBTRACTION, "tools" : qUnion([Q0, Q1]), "targets" : qUnion([Q2])});
        }
    });
